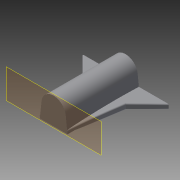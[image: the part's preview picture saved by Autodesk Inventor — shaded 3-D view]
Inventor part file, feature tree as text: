
AUTODESK INVENTOR PART (.ipt)
format: ipt  version: 2015 (Build 190159000, 159)  size: 1,705,984 bytes
history: native  units: in
note: dims shown in document units (in); Inventor stores cm internally (conversion verified against a paired STEP export)
features: sketch x29, plane x14, loft x11, extrude x9, fillet x6, other x3, projected_geometry x3, mirror x2, chamfer x2
ambient origin geometry x8: Origin, YZ Plane, XZ Plane, XY Plane, X Axis, Y Axis, Z Axis, Center Point
bodies: Solid1 (feature_tree)
feature tree (79):
  extrude  "Extrusion1"  TaperAngle=0.0deg  [1 undecoded]
  plane  "Work Plane1"
  plane  "Work Plane2"
  plane  "Work Plane3"
  loft  "Loft1"
  loft  "Loft2"
  fillet  "Fillet1"  Radius=240.6614in
  loft  "Loft4"
  fillet  "Fillet2"  Radius=125.0in
  extrude  "Extrusion2"  TaperAngle=0.0deg  [1 undecoded]
  extrude  "Extrusion3"  Depth=100.0in
  fillet  "Fillet3"  [1 undecoded]
  plane  "Work Plane4"
  mirror  "Mirror1"
  plane  "Work Plane5"
  sketch  "Sketch12"  dims[d36=0.0in d37=90.0deg d38=125.0in]
  loft  "Loft5"
  chamfer  "Chamfer1"  Angle=90.0deg  [1 undecoded]
  chamfer  "Chamfer2"  Angle=90.0deg  [1 undecoded]
  sketch  "Sketch15"  dims[d39=15.0in]
  plane  "Work Plane6"
  plane  "Work Plane7"
  loft  "Loft8"
  mirror  "Mirror2"
  extrude  "Extrusion5"  Depth=125.0in
  extrude  "Extrusion6"  TaperAngle=0.0deg  [1 undecoded]
  plane  "Work Plane8"
  sketch  "Sketch20"  dims[d51=10.0in]
  plane  "Work Plane10"
  loft  "Loft9"
  fillet  "Fillet4"  Radius=84.0in
  extrude  "Extrusion7"  Depth=0.6803in
  fillet  "Fillet5"  Radius=48.0in
  fillet  "Fillet6"  Radius=6500.0in
  sketch  "Sketch23"  dims[d55=0.0in]
  plane  "Work Plane11"
  sketch  "Sketch24"  dims[d56=0.0in]
  loft  "Loft10"
  loft  "Loft11"
  sketch  "Sketch27"  dims[d64=60.0in d70=125.0in]
  plane  "Work Plane12"
  loft  "Loft12"
  loft  "Loft13"
  loft  "Loft14"
  sketch  "Sketch31"  dims[d89=6500.0in d90=7700.0in]
  plane  "Work Plane13"
  sketch  "Sketch32"  dims[d91=10.0in d92=345.0in d93=0.0in]
  sketch  "Sketch33"  dims[d94=10.0in d95=125.0in]
  plane  "Work Plane14"
  extrude  "Extrusion8"  Depth=245.0in
  sketch  "Sketch35"  dims[d98=10.0in d99=0.0in]
  plane  "Work Plane15"
  extrude  "Extrusion9"  Depth=15.0in
  extrude  "Extrusion10"  Depth=0.0618in
  sketch  "Sketch1"  dims[d5=250.0in d12=0.0in]
  sketch  "Sketch2"  dims[d13=75.0in d15=110.0in]
  other  "Edges1"
  sketch  "Sketch3"  dims[d21=98.0in d24=110.0in d25=240.6614in]
  sketch  "Sketch6"  dims[d26=730.0in d27=0.0in d28=300.0in d29=125.0in]
  sketch  "Sketch7"  dims[d30=250.0in d31=0.0in]
  other  "Edges3"
  sketch  "Sketch8"  dims[d32=125.0in d33=100.0in d34=0.0in d35=90.0deg]
  other  "Edges4"
  sketch  "Sketch17"  dims[d40=20.0in]
  sketch  "Sketch18"  dims[d41=10.0in]
  sketch  "Sketch19"  dims[d50=15.0in]
  projected_geometry  "Projected Loop7"
  sketch  "Sketch21"  dims[d52=75.0in]
  sketch  "Sketch22"  dims[d54=125.0in]
  sketch  "Sketch25"  dims[d57=0.0in d58=0.0in d59=90.0deg d60=0.0in d61=90.0deg]
  sketch  "Sketch26"  dims[d62=10.65in d63=50.0in]
  sketch  "Sketch28"  dims[d71=50.0in d72=0.0in d73=90.0deg]
  sketch  "Sketch29"  dims[d74=0.0in d75=90.0deg d76=40.0in d79=84.0in]
  sketch  "Sketch30"  dims[d80=0.0in d82=0.6803in d83=48.0in d84=0.0in d85=6500.0in]
  sketch  "Sketch34"  dims[d96=200.0in d97=0.0in]
  projected_geometry  "Projected Loop8"
  projected_geometry  "Projected Loop9"
  sketch  "Sketch36"  dims[d100=0.0in d101=245.0in]
  sketch  "Sketch37"  dims[d102=90.0in d105=15.0in d106=0.0618in d107=45.0deg d108=345.0in d109=0.0in d110=90.0deg d111=0.0in d112=90.0deg d113=5.2in d114=0.125in d115=45.0deg d116=5.2in d117=0.125in d118=45.0deg d119=-200.0in d126=100.0in d127=25.0in d133=-205.0in d134=50.0in d135=60.0in d137=0.0in d138=90.0deg d139=0.0in d140=90.0deg d141=160.0in d142=100.0in d143=0.6528in d144=0.0in d145=0.0in d146=9000.0in d147=0.0in d148=15.0in d149=25.0in d150=0.0in d151=30.0in d152=0.0in d153=-20.0in d154=30.0in d155=10.0in d156=1.2162in d157=1.2162in d158=195.0in d160=225.0in d166=30.0in d167=225.0in d168=20.0in d169=30.0in d170=20.0in d171=80.0in d172=0.0in d173=90.0deg d174=0.0in d175=90.0deg d176=7.0in d177=0.1374in d178=200.0in d179=0.0in d180=9.475in d184=150.0in d185=150.0in d186=9.475in d187=40.0in d188=80.0in d189=65.0in d190=60.0in d191=20.0in d192=125.0in d193=0.0in d194=13.0in d195=32.0in d196=55.0in d197=55.0in d198=55.0in d199=80.0in d200=95.0in d201=95.0in d202=40.0in d203=0.0in d204=90.0deg d205=0.0in d206=90.0deg d207=0.0in d208=90.0deg d209=0.0in d210=90.0deg d211=25.0in d212=90.0in d213=8.0in d214=0.0in d215=90.0deg d216=0.0in d217=90.0deg d218=105.0in d219=5.0in d220=5.0in d221=0.0in d222=90.0deg d223=0.0in d224=90.0deg d225=105.0in d226=5.0in d227=5.0in d228=0.0in d229=90.0deg d230=0.0in d231=90.0deg d232=-20.0in d233=90.0deg d234=95.0in d235=0.0in d236=90.0deg d237=105.0in d238=0.0in d239=650.0in d240=0.0in]
note: 6 required parameter values undecoded (feature->parameter linkage not recoverable at this tier; creation-order binding heuristic only, values carry confidence <= 0.55)
